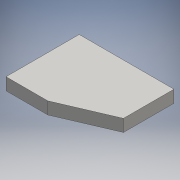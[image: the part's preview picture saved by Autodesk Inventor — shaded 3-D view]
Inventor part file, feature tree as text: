
AUTODESK INVENTOR PART (.ipt)
format: ipt  version: 2016 SP1 (Build 200210100, 210)  size: 105,984 bytes
history: native  units: mm
features: extrude x1, sketch x1
ambient origin geometry x8: Origin, YZ Plane, XZ Plane, XY Plane, X Axis, Y Axis, Z Axis, Center Point
bodies: Solid1 (feature_tree)
feature tree (2):
  extrude  "Extrusion1"  Depth=210.0mm
  sketch  "Sketch1"  dims[d0=272.0mm d1=210.0mm d2=105.0mm d3=136.0mm d4=120.0mm d5=145.0mm d6=35.0mm d7=0.0mm]
